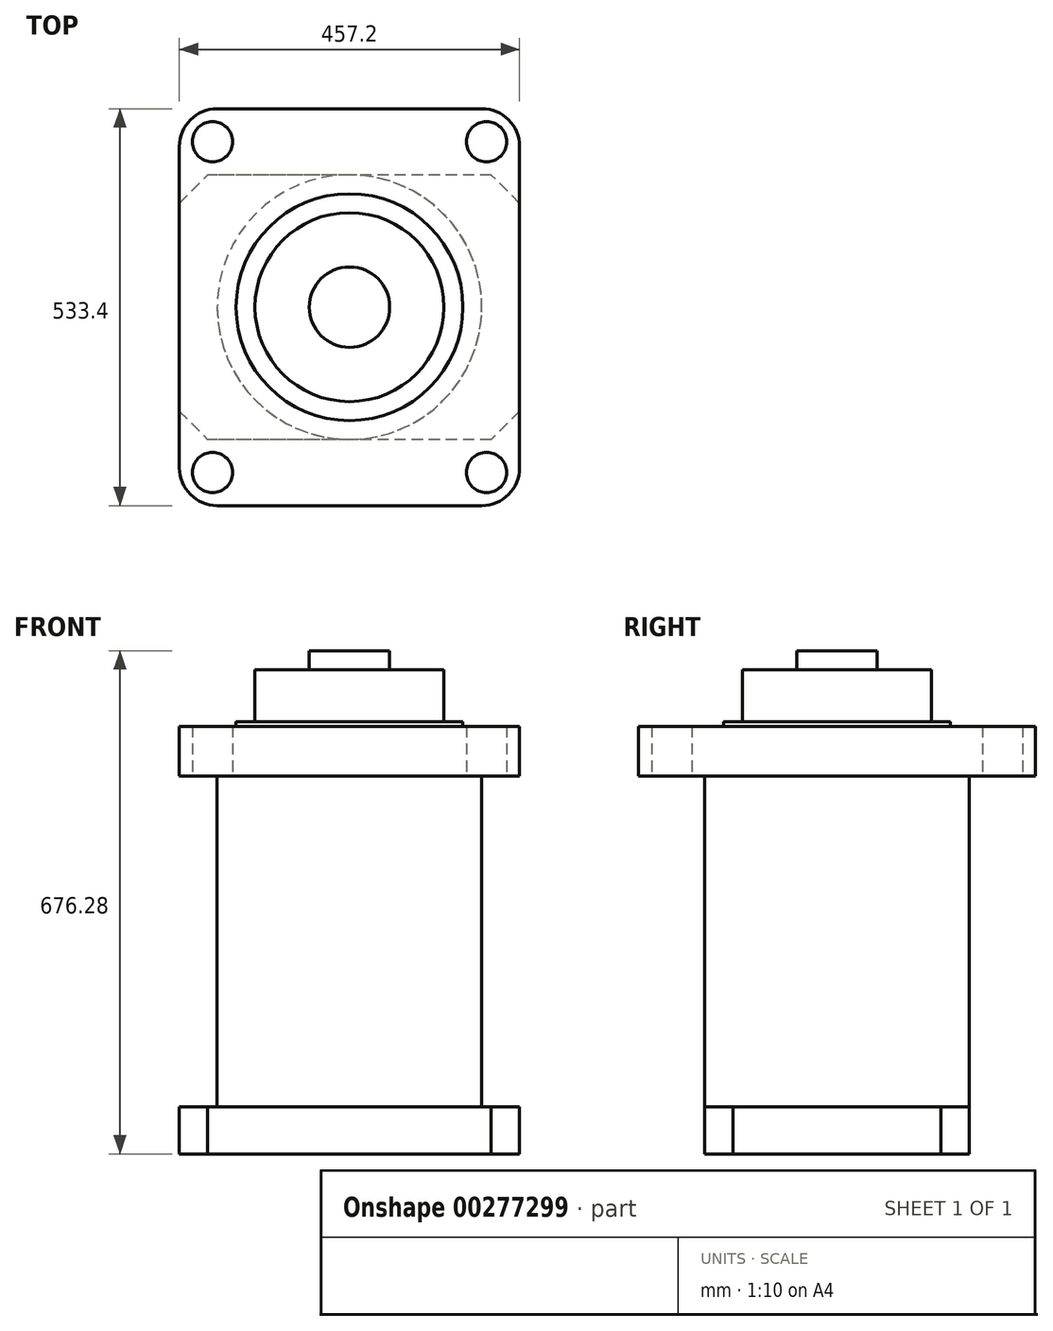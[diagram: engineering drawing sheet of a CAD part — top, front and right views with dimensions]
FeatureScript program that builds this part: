
annotation { "Feature Type Name" : "Feature", "Feature Type Description" : "" }
export const myFeature = defineFeature(function(context is Context, id is Id, definition is map)
    precondition{}
    {
        {
            var Q0;
            Q0=qCreatedBy(makeId("Top.planeOp"),FACE);
            var sketch = newSketch(context, id + "F0", { "sketchPlane" : qUnion([Q0])});
            skLineSegment(sketch, "E0.bottom", {"start": v(-177.8, 266.7) * mm, "end": v(177.8, 266.7) * mm});
            skLineSegment(sketch, "E0.top", {"start": v(-177.8, -266.7) * mm, "end": v(177.8, -266.7) * mm});
            skLineSegment(sketch, "E0.left", {"start": v(-228.6, 215.9) * mm, "end": v(-228.6, -215.9) * mm});
            skLineSegment(sketch, "E0.right", {"start": v(228.6, 215.9) * mm, "end": v(228.6, -215.9) * mm});
            skPoint(sketch, "E0.middle", {"position": v(0, 0) * mm});
            skPoint(sketch, "E1.visualSharp", {"position": v(-228.6, 266.7) * mm});
            skArc(sketch, "E1.filletArc", {"start": v(-177.8, 266.7) * mm, "mid": v(-213.72, 251.82) * mm, "end": v(-228.6, 215.9) * mm});
            skPoint(sketch, "E2.visualSharp", {"position": v(228.6, 266.7) * mm});
            skArc(sketch, "E2.filletArc", {"start": v(228.6, 215.9) * mm, "mid": v(213.72, 251.82) * mm, "end": v(177.8, 266.7) * mm});
            skPoint(sketch, "E3.visualSharp", {"position": v(228.6, -266.7) * mm});
            skArc(sketch, "E3.filletArc", {"start": v(177.8, -266.7) * mm, "mid": v(213.72, -251.82) * mm, "end": v(228.6, -215.9) * mm});
            skPoint(sketch, "E4.visualSharp", {"position": v(-228.6, -266.7) * mm});
            skArc(sketch, "E4.filletArc", {"start": v(-228.6, -215.9) * mm, "mid": v(-213.72, -251.82) * mm, "end": v(-177.8, -266.7) * mm});
            skLineSegment(sketch, "E5", {"start": v(-300.61, 0) * mm, "end": v(286.14, 0) * mm, "construction": true});
            skPoint(sketch, "E5.endSnap0", {"position": v(-228.6, 0) * mm});
            skLineSegment(sketch, "E6", {"start": v(0, 325.49) * mm, "end": v(0, -313.3) * mm, "construction": true});
            skPoint(sketch, "E6.endSnap0", {"position": v(0, -266.7) * mm});
            skLineSegment(sketch, "E7.0", {"start": v(-184.15, 325.49) * mm, "end": v(-184.15, -313.3) * mm, "construction": true});
            skLineSegment(sketch, "E8.0", {"start": v(-300.61, -222.25) * mm, "end": v(286.14, -222.25) * mm, "construction": true});
            skCircle(sketch, "E9", {"center": v(-184.15, -222.25) * mm, "radius": 26.99 * mm});
            skCircle(sketch, "E10.MirrorC", {"center": v(184.15, -222.25) * mm, "radius": 26.99 * mm});
            skCircle(sketch, "E11.MirrorC", {"center": v(-184.15, 222.25) * mm, "radius": 26.99 * mm});
            skCircle(sketch, "E12.MirrorC", {"center": v(184.15, 222.25) * mm, "radius": 26.99 * mm});
            skSolve(sketch);
        }
        {
            var Q0;
            Q0 = qSketchRegion(id + "F0", true);
            extrude(context, id + "F1", {"entities" : qUnion([Q0]), "depth" : 66.67 * mm});
        }
        {
            var Q0;
            Q0=makeQuery(id+"F1.opExtrude","CAP_FACE",FACE,{"disambiguationData":[OSD([sQuery(id+"F0.wireOp",EDGE,"E0.bottom"),sQuery(id+"F0.wireOp",EDGE,"E0.top"),sQuery(id+"F0.wireOp",EDGE,"E0.left"),sQuery(id+"F0.wireOp",EDGE,"E0.right"),sQuery(id+"F0.wireOp",EDGE,"E1.filletArc"),sQuery(id+"F0.wireOp",EDGE,"E2.filletArc"),sQuery(id+"F0.wireOp",EDGE,"E3.filletArc"),sQuery(id+"F0.wireOp",EDGE,"E4.filletArc"),sQuery(id+"F0.wireOp",EDGE,"E9"),sQuery(id+"F0.wireOp",EDGE,"E10.MirrorC"),sQuery(id+"F0.wireOp",EDGE,"E11.MirrorC"),sQuery(id+"F0.wireOp",EDGE,"E12.MirrorC")])],"isStart":false});
            var sketch = newSketch(context, id + "F2", { "sketchPlane" : qUnion([Q0])});
            skCircle(sketch, "E13", {"center": v(0, 0) * mm, "radius": 152.4 * mm});
            skSolve(sketch);
        }
        {
            var Q0;
            Q0 = qSketchRegion(id + "F2", true);
            extrude(context, id + "F3", {"entities" : qUnion([Q0]), "operationType" : NewBodyOperationType.ADD, "depth" : 6.35 * mm});
        }
        {
            var Q0;
            Q0=makeQuery(id+"F1.opExtrude","CAP_FACE",FACE,{"disambiguationData":[OSD([sQuery(id+"F0.wireOp",EDGE,"E0.bottom"),sQuery(id+"F0.wireOp",EDGE,"E0.top"),sQuery(id+"F0.wireOp",EDGE,"E0.left"),sQuery(id+"F0.wireOp",EDGE,"E0.right"),sQuery(id+"F0.wireOp",EDGE,"E1.filletArc"),sQuery(id+"F0.wireOp",EDGE,"E2.filletArc"),sQuery(id+"F0.wireOp",EDGE,"E3.filletArc"),sQuery(id+"F0.wireOp",EDGE,"E4.filletArc"),sQuery(id+"F0.wireOp",EDGE,"E9"),sQuery(id+"F0.wireOp",EDGE,"E10.MirrorC"),sQuery(id+"F0.wireOp",EDGE,"E11.MirrorC"),sQuery(id+"F0.wireOp",EDGE,"E12.MirrorC")])],"isStart":false});
            var sketch = newSketch(context, id + "F4", { "sketchPlane" : qUnion([Q0])});
            skCircle(sketch, "E14", {"center": v(0, 0) * mm, "radius": 127 * mm});
            skSolve(sketch);
        }
        {
            var Q0;
            Q0 = qSketchRegion(id + "F4", true);
            extrude(context, id + "F5", {"entities" : qUnion([Q0]), "operationType" : NewBodyOperationType.ADD, "depth" : 76.2 * mm});
        }
        {
            var Q0;
            Q0=makeQuery(id+"F5.opExtrude","CAP_FACE",FACE,{"disambiguationData":[OSD([sQuery(id+"F4.wireOp",EDGE,"E14")])],"isStart":false});
            var sketch = newSketch(context, id + "F6", { "sketchPlane" : qUnion([Q0])});
            skCircle(sketch, "E15", {"center": v(0, 0) * mm, "radius": 53.98 * mm});
            skSolve(sketch);
        }
        {
            var Q0;
            Q0 = qSketchRegion(id + "F6", true);
            extrude(context, id + "F7", {"entities" : qUnion([Q0]), "operationType" : NewBodyOperationType.ADD, "depth" : 25.4 * mm});
        }
        {
            var Q0;
            Q0=makeQuery(id+"F1.opExtrude","CAP_FACE",FACE,{"disambiguationData":[OSD([sQuery(id+"F0.wireOp",EDGE,"E0.bottom"),sQuery(id+"F0.wireOp",EDGE,"E0.top"),sQuery(id+"F0.wireOp",EDGE,"E0.left"),sQuery(id+"F0.wireOp",EDGE,"E0.right"),sQuery(id+"F0.wireOp",EDGE,"E1.filletArc"),sQuery(id+"F0.wireOp",EDGE,"E2.filletArc"),sQuery(id+"F0.wireOp",EDGE,"E3.filletArc"),sQuery(id+"F0.wireOp",EDGE,"E4.filletArc"),sQuery(id+"F0.wireOp",EDGE,"E9"),sQuery(id+"F0.wireOp",EDGE,"E10.MirrorC"),sQuery(id+"F0.wireOp",EDGE,"E11.MirrorC"),sQuery(id+"F0.wireOp",EDGE,"E12.MirrorC")])],"isStart":true});
            var sketch = newSketch(context, id + "F8", { "sketchPlane" : qUnion([Q0])});
            skCircle(sketch, "E16", {"center": v(0, 0) * mm, "radius": 177.8 * mm});
            skSolve(sketch);
        }
        {
            var Q0;
            Q0 = qSketchRegion(id + "F8", true);
            extrude(context, id + "F9", {"entities" : qUnion([Q0]), "operationType" : NewBodyOperationType.ADD, "depth" : 508 * mm});
        }
        {
            var Q0;
            Q0=makeQuery(id+"F9.opExtrude","CAP_FACE",FACE,{"disambiguationData":[OSD([sQuery(id+"F8.wireOp",EDGE,"E16")])],"isStart":false});
            var sketch = newSketch(context, id + "F10", { "sketchPlane" : qUnion([Q0])});
            skLineSegment(sketch, "E17.bottom", {"start": v(228.6, -177.8) * mm, "end": v(-228.6, -177.8) * mm});
            skLineSegment(sketch, "E17.top", {"start": v(228.6, 177.8) * mm, "end": v(-228.6, 177.8) * mm});
            skLineSegment(sketch, "E17.left", {"start": v(228.6, -177.8) * mm, "end": v(228.6, 177.8) * mm});
            skLineSegment(sketch, "E17.right", {"start": v(-228.6, -177.8) * mm, "end": v(-228.6, 177.8) * mm});
            skPoint(sketch, "E17.middle", {"position": v(0, 0) * mm});
            skSolve(sketch);
        }
        {
            var Q0;
            Q0 = qSketchRegion(id + "F10", true);
            extrude(context, id + "F11", {"entities" : qUnion([Q0]), "operationType" : NewBodyOperationType.ADD, "oppositeDirection" : true, "depth" : 63.5 * mm});
        }
        {
            var Q0;
            Q0=makeQuery(id+"F11.opExtrude","SWEPT_EDGE",EDGE,{"disambiguationData":[OSD([sQuery(id+"F10.wireOp",EDGE,"E17.top"),sQuery(id+"F10.wireOp",EDGE,"E17.left")])]});
            var Q1;
            Q1=makeQuery(id+"F11.opExtrude","SWEPT_EDGE",EDGE,{"disambiguationData":[OSD([sQuery(id+"F10.wireOp",EDGE,"E17.top"),sQuery(id+"F10.wireOp",EDGE,"E17.right")])]});
            var Q2;
            Q2=makeQuery(id+"F11.opExtrude","SWEPT_EDGE",EDGE,{"disambiguationData":[OSD([sQuery(id+"F10.wireOp",EDGE,"E17.bottom"),sQuery(id+"F10.wireOp",EDGE,"E17.left")])]});
            var Q3;
            Q3=makeQuery(id+"F11.opExtrude","SWEPT_EDGE",EDGE,{"disambiguationData":[OSD([sQuery(id+"F10.wireOp",EDGE,"E17.bottom"),sQuery(id+"F10.wireOp",EDGE,"E17.right")])]});
            chamfer(context, id + "F12", {"entities" : qUnion([Q0, Q1, Q2, Q3]), "width" : 38.1 * mm, "tangentPropagation" : true});
        }
    });
